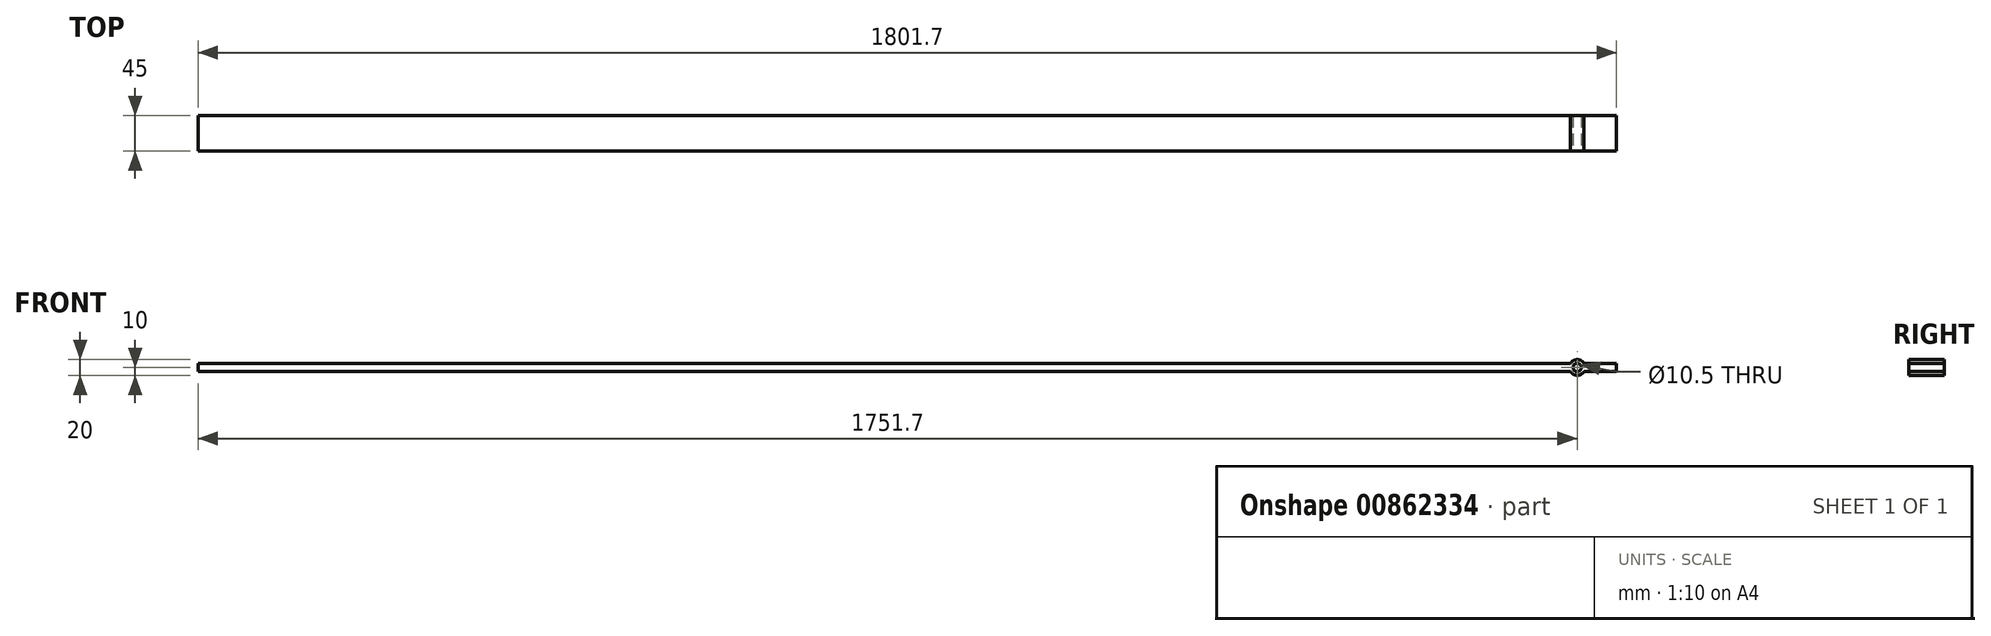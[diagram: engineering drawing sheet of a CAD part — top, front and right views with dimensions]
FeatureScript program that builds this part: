
annotation { "Feature Type Name" : "Feature", "Feature Type Description" : "" }
export const myFeature = defineFeature(function(context is Context, id is Id, definition is map)
    precondition{}
    {
        {
            var Q0;
            Q0=qCreatedBy(makeId("Front.planeOp"),FACE);
            var sketch = newSketch(context, id + "F0", { "sketchPlane" : qUnion([Q0])});
            skLineSegment(sketch, "E0.bottom", {"start": v(-1801.7, 5) * mm, "end": v(-58.66, 5) * mm});
            skLineSegment(sketch, "E0.top", {"start": v(-1801.7, -5) * mm, "end": v(-58.66, -5) * mm});
            skLineSegment(sketch, "E0.left", {"start": v(-1801.7, 5) * mm, "end": v(-1801.7, -5) * mm});
            skLineSegment(sketch, "E0.right", {"start": v(0, 5) * mm, "end": v(0, -5) * mm});
            skCircle(sketch, "E1", {"center": v(-50, 0) * mm, "radius": 10 * mm});
            skLineSegment(sketch, "E2.trimOffspring", {"start": v(-41.34, 5) * mm, "end": v(0, 5) * mm});
            skLineSegment(sketch, "E3.trimOffspring", {"start": v(-41.34, -5) * mm, "end": v(0, -5) * mm});
            skSolve(sketch);
        }
        {
            var Q0;
            Q0 = qSketchRegion(id + "F0", true);
            extrude(context, id + "F1", {"entities" : qUnion([Q0]), "depth" : 45 * mm, "offsetDistance" : 25 * mm});
        }
        {
            var Q0;
            Q0=makeQuery(id+"F1.opExtrude","CAP_FACE",FACE,{"disambiguationData":[OSD([sQuery(id+"F0.wireOp",EDGE,"E0.bottom"),sQuery(id+"F0.wireOp",EDGE,"E0.top"),sQuery(id+"F0.wireOp",EDGE,"E0.left"),sQuery(id+"F0.wireOp",EDGE,"E0.right"),sQuery(id+"F0.wireOp",EDGE,"E1"),sQuery(id+"F0.wireOp",EDGE,"E2.trimOffspring"),sQuery(id+"F0.wireOp",EDGE,"E3.trimOffspring")])],"isStart":false});
            var sketch = newSketch(context, id + "F2", { "sketchPlane" : qUnion([Q0])});
            skCircle(sketch, "E4", {"center": v(-50, 0) * mm, "radius": 2.86 * mm});
            skSolve(sketch);
        }
        {
            var Q0;
            Q0=sQuery(id+"F2.wireOp",VERTEX,"E4.center");
            var Q1;
            Q1=makeQuery(id+"F1.opExtrude","SWEPT_BODY",BODY,{"disambiguationData":[OSD([sQuery(id+"F0.wireOp",EDGE,"E0.bottom"),sQuery(id+"F0.wireOp",EDGE,"E0.top"),sQuery(id+"F0.wireOp",EDGE,"E0.left"),sQuery(id+"F0.wireOp",EDGE,"E0.right"),sQuery(id+"F0.wireOp",EDGE,"E1"),sQuery(id+"F0.wireOp",EDGE,"E2.trimOffspring"),sQuery(id+"F0.wireOp",EDGE,"E3.trimOffspring")])]});
            hole(context, id + "F3", {"style" : HoleStyle.SIMPLE, "endStyle" : HoleEndStyle.THROUGH, "standardTappedOrClearance" : lookupTablePath({ "standard" : "ISO", "engagement" : "75%", "pitch" : "1.5 mm", "size" : "M12", "type" : "Tapped" }), "standardBlindInLast" : lookupTablePath({ "standard" : "ISO", "engagement" : "75%", "pitch" : "1.5 mm", "size" : "M12", "type" : "Tapped" }), "holeDiameter" : 10.5 * mm, "majorDiameter" : 12 * mm, "showTappedDepth" : true, "isTappedThrough" : true, "tappedDepth" : 12 * mm, "tapClearance" : 3, "locations" : qUnion([Q0]), "scope" : qUnion([Q1])});
        }
    });
